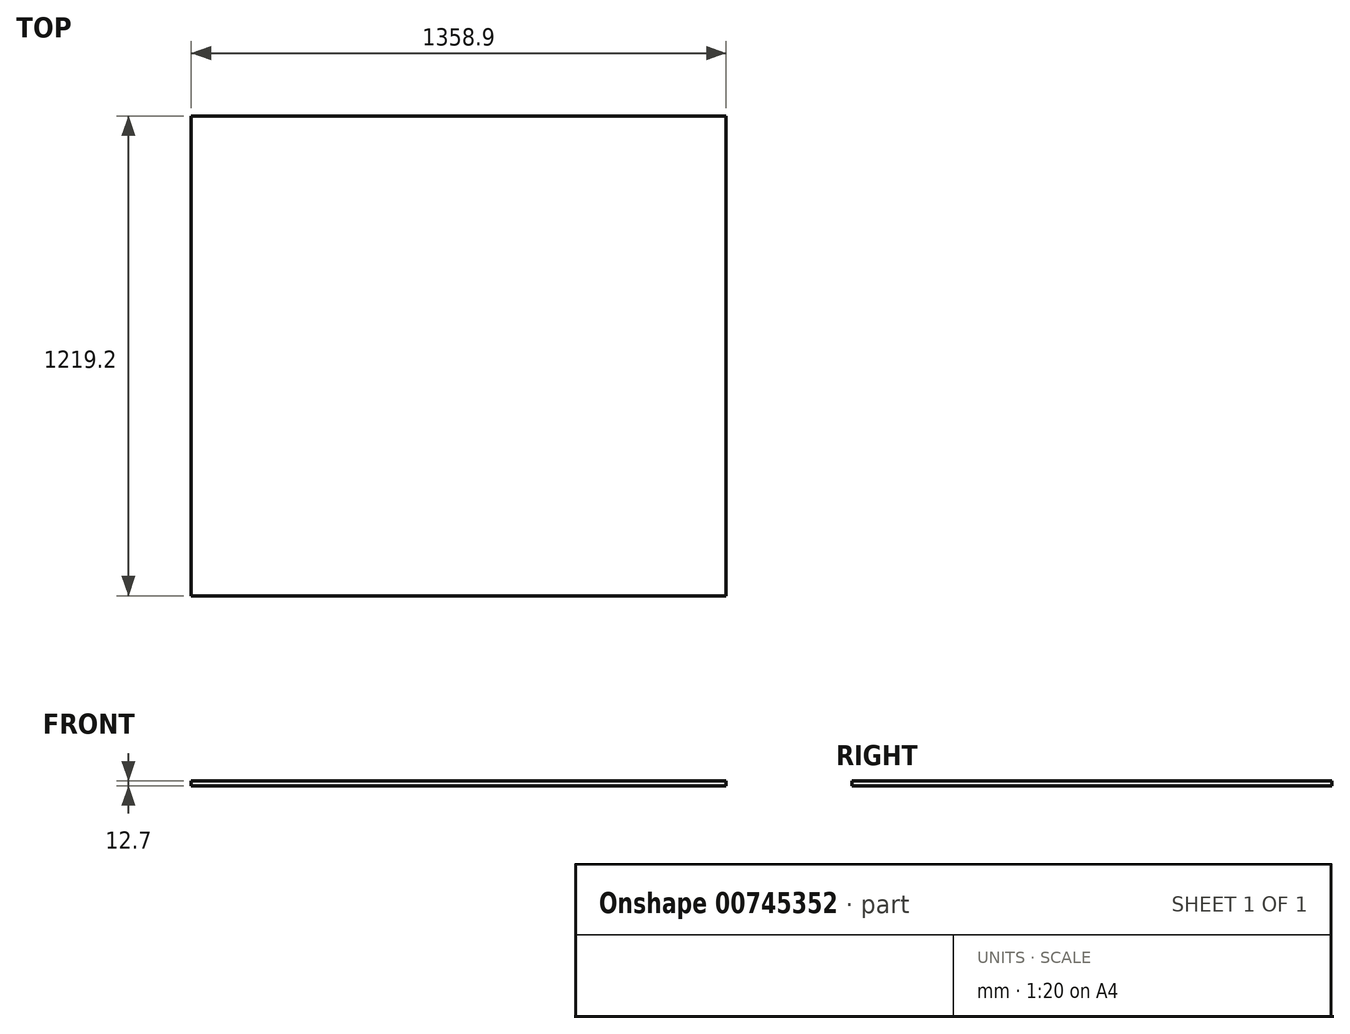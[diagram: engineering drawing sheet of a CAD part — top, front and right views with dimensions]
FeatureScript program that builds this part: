
annotation { "Feature Type Name" : "Feature", "Feature Type Description" : "" }
export const myFeature = defineFeature(function(context is Context, id is Id, definition is map)
    precondition{}
    {
        {
            var Q0;
            Q0=qCreatedBy(makeId("Top.planeOp"),FACE);
            var sketch = newSketch(context, id + "F0", { "sketchPlane" : qUnion([Q0])});
            skLineSegment(sketch, "E0.bottom", {"start": v(0, 0) * mm, "end": v(1358.9, 0) * mm});
            skLineSegment(sketch, "E0.top", {"start": v(0, 1219.2) * mm, "end": v(1358.9, 1219.2) * mm});
            skLineSegment(sketch, "E0.left", {"start": v(0, 0) * mm, "end": v(0, 1219.2) * mm});
            skLineSegment(sketch, "E0.right", {"start": v(1358.9, 0) * mm, "end": v(1358.9, 1219.2) * mm});
            skSolve(sketch);
        }
        {
            var Q0;
            Q0=makeQuery(id+"F0.imprint","IMPRINT",FACE,{"disambiguationData":[TD([[makeQuery(id+"F0.imprint","IMPRINT",EDGE,{"derivedFrom":sQuery(id+"F0.wireOp",EDGE,"XOJL2qkw-726g-F02Q-CQMI-GWsZiQ8f43vg.bottom")}),1.0]])]});
            var Q1;
            Q1=makeQuery(id+"F0.imprint","IMPRINT",FACE,{"disambiguationData":[TD([[makeQuery(id+"F0.imprint","IMPRINT",EDGE,{"derivedFrom":sQuery(id+"F0.wireOp",EDGE,"E0.bottom")}),1.0]])]});
            extrude(context, id + "F1", {"entities" : qUnion([Q0, Q1]), "depth" : 12.7 * mm, "offsetDistance" : 25.4 * mm});
        }
    });
